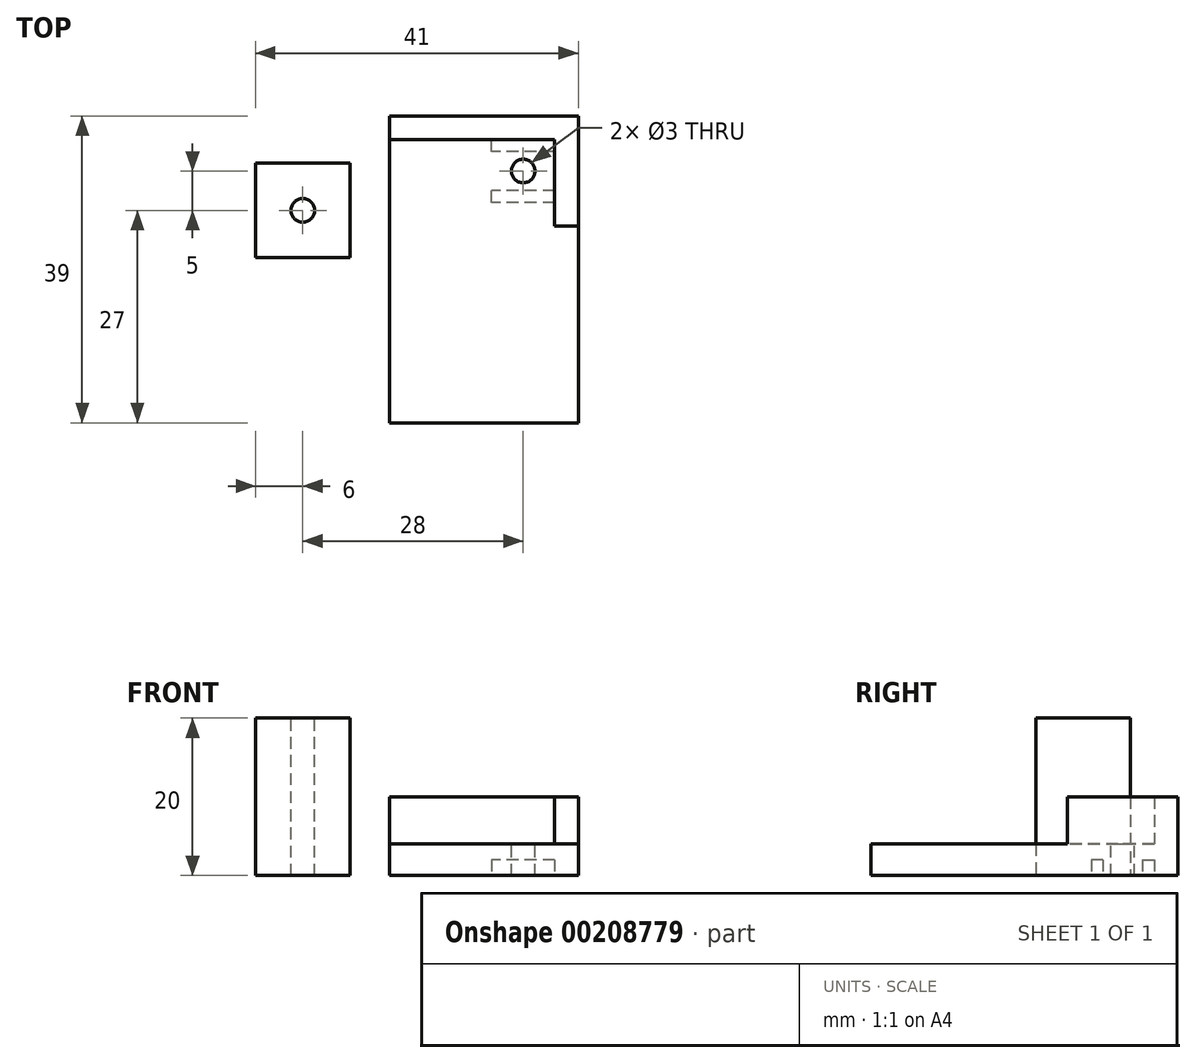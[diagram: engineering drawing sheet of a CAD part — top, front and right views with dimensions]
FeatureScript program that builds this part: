
annotation { "Feature Type Name" : "Feature", "Feature Type Description" : "" }
export const myFeature = defineFeature(function(context is Context, id is Id, definition is map)
    precondition{}
    {
        {
            var Q0;
            Q0=qCreatedBy(makeId("Top.planeOp"),FACE);
            var sketch = newSketch(context, id + "F0", { "sketchPlane" : qUnion([Q0])});
            skLineSegment(sketch, "E0.bottom", {"start": v(12, -12) * mm, "end": v(-12, -12) * mm});
            skLineSegment(sketch, "E0.top", {"start": v(12, 12) * mm, "end": v(-12, 12) * mm});
            skLineSegment(sketch, "E0.left", {"start": v(12, -12) * mm, "end": v(12, 12) * mm});
            skLineSegment(sketch, "E0.right", {"start": v(-12, -12) * mm, "end": v(-12, 12) * mm});
            skPoint(sketch, "E0.middle", {"position": v(0, 0) * mm});
            skLineSegment(sketch, "E1", {"start": v(-12, -12) * mm, "end": v(-12, -27) * mm});
            skLineSegment(sketch, "E2", {"start": v(-12, -27) * mm, "end": v(12, -27) * mm});
            skLineSegment(sketch, "E3", {"start": v(12, -27) * mm, "end": v(12, -12) * mm});
            skSolve(sketch);
        }
        {
            var Q0;
            Q0=makeQuery(id+"F0.imprint","IMPRINT",FACE,{"disambiguationData":[TD([[makeQuery(id+"F0.imprint","IMPRINT",EDGE,{"derivedFrom":sQuery(id+"F0.wireOp",EDGE,"E0.bottom")}),-1.0]])]});
            var Q1;
            Q1=makeQuery(id+"F0.imprint","IMPRINT",FACE,{"disambiguationData":[TD([[makeQuery(id+"F0.imprint","IMPRINT",EDGE,{"derivedFrom":sQuery(id+"F0.wireOp",EDGE,"E0.bottom")}),1.0]])]});
            extrude(context, id + "F1", {"entities" : qUnion([Q0, Q1]), "depth" : 4 * mm});
        }
        {
            var Q0;
            Q0=makeQuery(id+"F1.opExtrude","CAP_FACE",FACE,{"disambiguationData":[OSD([sQuery(id+"F0.wireOp",EDGE,"E0.bottom"),sQuery(id+"F0.wireOp",EDGE,"E0.top"),sQuery(id+"F0.wireOp",EDGE,"E0.left"),sQuery(id+"F0.wireOp",EDGE,"E0.right")])],"isStart":false});
            var sketch = newSketch(context, id + "F2", { "sketchPlane" : qUnion([Q0])});
            skLineSegment(sketch, "E4", {"start": v(-12, 12) * mm, "end": v(-12, 9) * mm});
            skLineSegment(sketch, "E5", {"start": v(-12, 9) * mm, "end": v(9, 9) * mm});
            skLineSegment(sketch, "E6", {"start": v(12, 12) * mm, "end": v(-12, 12) * mm});
            skLineSegment(sketch, "E7", {"start": v(9, 9) * mm, "end": v(9, -2) * mm});
            skLineSegment(sketch, "E8", {"start": v(9, -2) * mm, "end": v(12, -2) * mm});
            skLineSegment(sketch, "E9", {"start": v(12, -2) * mm, "end": v(12, 12) * mm});
            skSolve(sketch);
        }
        {
            var Q0;
            Q0=makeQuery(id+"F2.imprint","IMPRINT",FACE,{"disambiguationData":[TD([[makeQuery(id+"F2.imprint","IMPRINT",EDGE,{"derivedFrom":sQuery(id+"F2.wireOp",EDGE,"E4")}),-1.0]])]});
            extrude(context, id + "F3", {"entities" : qUnion([Q0]), "operationType" : NewBodyOperationType.ADD, "depth" : 6 * mm});
        }
        {
            var Q0;
            Q0=makeQuery(id+"F0.imprint","IMPRINT",FACE,{"disambiguationData":[TD([[makeQuery(id+"F0.imprint","IMPRINT",EDGE,{"derivedFrom":sQuery(id+"F0.wireOp",EDGE,"E0.bottom")}),-1.0]])]});
            var sketch = newSketch(context, id + "F4", { "sketchPlane" : qUnion([Q0])});
            skLineSegment(sketch, "E10", {"start": v(9, 1) * mm, "end": v(1, 1) * mm});
            skLineSegment(sketch, "E11", {"start": v(1, 1) * mm, "end": v(1, 2.5) * mm});
            skLineSegment(sketch, "E12", {"start": v(1, 2.5) * mm, "end": v(1, 7.5) * mm, "construction": true});
            skLineSegment(sketch, "E13", {"start": v(1, 7.5) * mm, "end": v(1, 9) * mm});
            skLineSegment(sketch, "E14", {"start": v(1, 9) * mm, "end": v(9, 9) * mm});
            skLineSegment(sketch, "E15", {"start": v(9, 9) * mm, "end": v(9, 7.5) * mm});
            skLineSegment(sketch, "E16", {"start": v(9, 7.5) * mm, "end": v(9, 2.5) * mm, "construction": true});
            skLineSegment(sketch, "E17", {"start": v(9, 2.5) * mm, "end": v(9, 1) * mm});
            skLineSegment(sketch, "E18", {"start": v(9, 2.5) * mm, "end": v(1, 2.5) * mm});
            skLineSegment(sketch, "E19", {"start": v(9, 7.5) * mm, "end": v(1, 7.5) * mm});
            skLineSegment(sketch, "E20", {"start": v(1, 5) * mm, "end": v(5, 5) * mm});
            skPoint(sketch, "E20.endSnap0", {"position": v(5, 7.5) * mm});
            skLineSegment(sketch, "E21", {"start": v(5, 5) * mm, "end": v(9, 5) * mm});
            skSolve(sketch);
        }
        {
            var Q0;
            Q0=qSketchRegion(id+"F4",true);
            extrude(context, id + "F5", {"entities" : qUnion([Q0]), "operationType" : NewBodyOperationType.REMOVE, "depth" : 2 * mm});
        }
        {
            var Q0;
            Q0=sQuery(id+"F4.wireOp",VERTEX,"E20.end");
            var Q1;
            Q1=makeQuery(id+"F1.opExtrude","SWEPT_BODY",BODY,{"disambiguationData":[OSD([sQuery(id+"F0.wireOp",EDGE,"E0.bottom"),sQuery(id+"F0.wireOp",EDGE,"E0.top"),sQuery(id+"F0.wireOp",EDGE,"E0.left"),sQuery(id+"F0.wireOp",EDGE,"E0.right")])]});
            hole(context, id + "F6", {"style" : HoleStyle.SIMPLE, "endStyle" : HoleEndStyle.THROUGH, "oppositeDirection" : true, "holeDiameter" : 3 * mm, "locations" : qUnion([Q0]), "scope" : qUnion([Q1]), "isTappedThrough" : true});
        }
        {
            var Q0;
            Q0=qCreatedBy(makeId("Top.planeOp"),FACE);
            var sketch = newSketch(context, id + "F7", { "sketchPlane" : qUnion([Q0])});
            skLineSegment(sketch, "E22", {"start": v(-17, -6) * mm, "end": v(-17, 6) * mm});
            skLineSegment(sketch, "E23", {"start": v(-17, 6) * mm, "end": v(-29, 6) * mm});
            skLineSegment(sketch, "E24", {"start": v(-29, 6) * mm, "end": v(-29, -6) * mm});
            skLineSegment(sketch, "E25", {"start": v(-29, -6) * mm, "end": v(-17, -6) * mm});
            skPoint(sketch, "E26", {"position": v(-23, 0) * mm});
            skPoint(sketch, "E26.positionSnap0", {"position": v(-17, 0) * mm});
            skPoint(sketch, "E26.positionSnap1", {"position": v(-23, 6) * mm});
            skSolve(sketch);
        }
        {
            var Q0;
            Q0=makeQuery(id+"F7.imprint","IMPRINT",FACE,{"disambiguationData":[TD([[makeQuery(id+"F7.imprint","IMPRINT",EDGE,{"derivedFrom":sQuery(id+"F7.wireOp",EDGE,"E22")}),1.0]])]});
            extrude(context, id + "F8", {"entities" : qUnion([Q0]), "depth" : 20 * mm});
        }
        {
            var Q0;
            Q0=makeQuery(id+"F8.opExtrude","CAP_FACE",FACE,{"disambiguationData":[OSD([sQuery(id+"F7.wireOp",EDGE,"E22"),sQuery(id+"F7.wireOp",EDGE,"E23"),sQuery(id+"F7.wireOp",EDGE,"E24"),sQuery(id+"F7.wireOp",EDGE,"E25")])],"isStart":false});
            var sketch = newSketch(context, id + "F9", { "sketchPlane" : qUnion([Q0])});
            skLineSegment(sketch, "E27", {"start": v(-19, -4) * mm, "end": v(-27, -4) * mm});
            skLineSegment(sketch, "E28", {"start": v(-27, -4) * mm, "end": v(-27, -2.5) * mm});
            skLineSegment(sketch, "E29", {"start": v(-27, -2.5) * mm, "end": v(-27, 2.5) * mm, "construction": true});
            skLineSegment(sketch, "E30", {"start": v(-27, 2.5) * mm, "end": v(-27, 4) * mm});
            skLineSegment(sketch, "E31", {"start": v(-27, 4) * mm, "end": v(-19, 4) * mm});
            skLineSegment(sketch, "E32", {"start": v(-19, 4) * mm, "end": v(-19, 2.5) * mm});
            skLineSegment(sketch, "E33", {"start": v(-19, 2.5) * mm, "end": v(-19, -2.5) * mm, "construction": true});
            skLineSegment(sketch, "E34", {"start": v(-19, -2.5) * mm, "end": v(-19, -4) * mm});
            skLineSegment(sketch, "E35", {"start": v(-19, -2.5) * mm, "end": v(-27, -2.5) * mm});
            skLineSegment(sketch, "E36", {"start": v(-27, 2.5) * mm, "end": v(-19, 2.5) * mm});
            skLineSegment(sketch, "E37", {"start": v(-17, 0) * mm, "end": v(-19, 0) * mm, "construction": true});
            skLineSegment(sketch, "E38", {"start": v(-23, -6) * mm, "end": v(-23, -4) * mm, "construction": true});
            skSolve(sketch);
        }
        {
            var Q0;
            Q0=sQuery(id+"F7.wireOp",VERTEX,"E26");
            var Q1;
            Q1=makeQuery(id+"F8.opExtrude","SWEPT_BODY",BODY,{"disambiguationData":[OSD([sQuery(id+"F7.wireOp",EDGE,"E22"),sQuery(id+"F7.wireOp",EDGE,"E23"),sQuery(id+"F7.wireOp",EDGE,"E24"),sQuery(id+"F7.wireOp",EDGE,"E25")])]});
            hole(context, id + "F10", {"style" : HoleStyle.SIMPLE, "endStyle" : HoleEndStyle.THROUGH, "oppositeDirection" : true, "holeDiameter" : 3 * mm, "locations" : qUnion([Q0]), "scope" : qUnion([Q1]), "isTappedThrough" : true});
        }
    });
